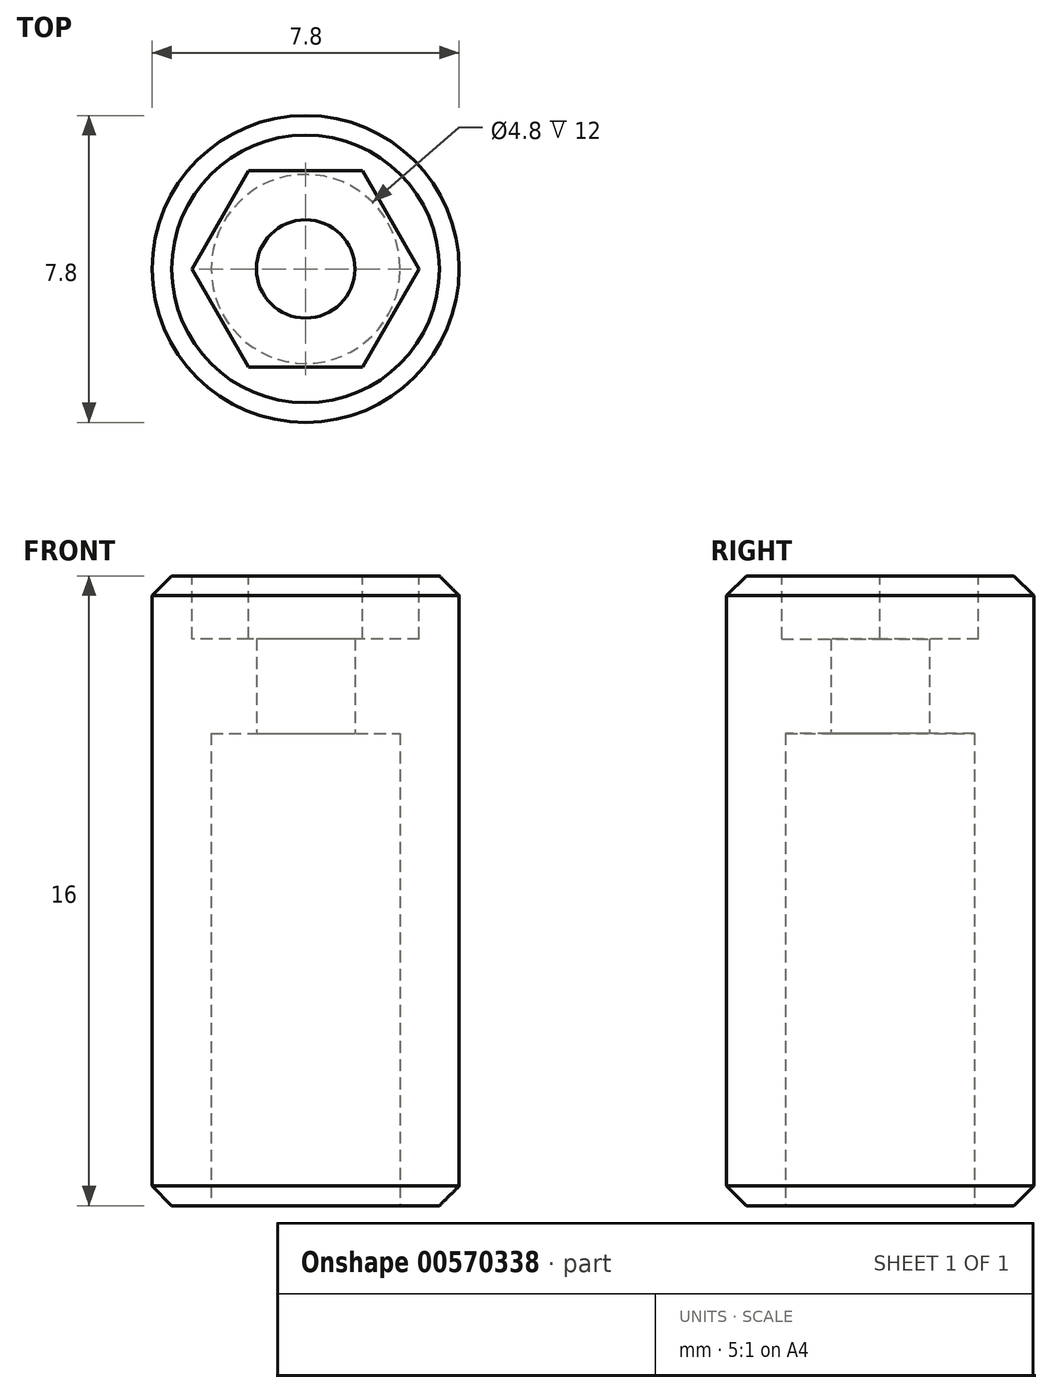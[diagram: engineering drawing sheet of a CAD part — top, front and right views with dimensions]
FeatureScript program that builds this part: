
annotation { "Feature Type Name" : "Feature", "Feature Type Description" : "" }
export const myFeature = defineFeature(function(context is Context, id is Id, definition is map)
    precondition{}
    {
        {
            var Q0;
            Q0=qCreatedBy(makeId("Top.planeOp"),FACE);
            var sketch = newSketch(context, id + "F0", { "sketchPlane" : qUnion([Q0])});
            skCircle(sketch, "E0", {"center": v(0, 0) * mm, "radius": 3.9 * mm});
            skSolve(sketch);
        }
        {
            var Q0;
            Q0 = qSketchRegion(id + "F0", true);
            extrude(context, id + "F1", {"entities" : qUnion([Q0]), "depth" : 16 * mm, "offsetDistance" : 25 * mm});
        }
        {
            var Q0;
            Q0=makeQuery(id+"F1.opExtrude","CAP_FACE",FACE,{"disambiguationData":[OSD([sQuery(id+"F0.wireOp",EDGE,"E0")])],"isStart":true});
            var sketch = newSketch(context, id + "F2", { "sketchPlane" : qUnion([Q0])});
            skCircle(sketch, "E1", {"center": v(0, 0) * mm, "radius": 2.4 * mm});
            skSolve(sketch);
        }
        {
            var Q0;
            Q0 = qSketchRegion(id + "F2", true);
            extrude(context, id + "F3", {"entities" : qUnion([Q0]), "operationType" : NewBodyOperationType.REMOVE, "oppositeDirection" : true, "depth" : 12 * mm, "offsetDistance" : 25 * mm});
        }
        {
            var Q0;
            Q0=makeQuery(id+"F3.boolean.opBoolean","COPY",FACE,{"derivedFrom":makeQuery(id+"F3.opExtrude","CAP_FACE",FACE,{"disambiguationData":[OSD([sQuery(id+"F2.wireOp",EDGE,"E1")])],"isStart":false})});
            var sketch = newSketch(context, id + "F4", { "sketchPlane" : qUnion([Q0])});
            skCircle(sketch, "E2", {"center": v(0, 0) * mm, "radius": 1.25 * mm});
            skSolve(sketch);
        }
        {
            var Q0;
            Q0 = qSketchRegion(id + "F4", true);
            extrude(context, id + "F5", {"entities" : qUnion([Q0]), "operationType" : NewBodyOperationType.REMOVE, "endBound" : BoundingType.THROUGH_ALL, "oppositeDirection" : true, "depth" : 25 * mm, "offsetDistance" : 25 * mm});
        }
        {
            var Q0;
            Q0=makeQuery(id+"F1.opExtrude","CAP_EDGE",EDGE,{"disambiguationData":[OSD([sQuery(id+"F0.wireOp",EDGE,"E0")])],"isStart":false});
            chamfer(context, id + "F6", {"entities" : qUnion([Q0]), "width" : .5 * mm, "tangentPropagation" : true});
        }
        {
            var Q0;
            Q0=makeQuery(id+"F1.opExtrude","CAP_EDGE",EDGE,{"disambiguationData":[OSD([sQuery(id+"F0.wireOp",EDGE,"E0")])],"isStart":true});
            chamfer(context, id + "F7", {"entities" : qUnion([Q0]), "width" : .5 * mm, "tangentPropagation" : true});
        }
        {
            var Q0;
            Q0=makeQuery(id+"F1.opExtrude","CAP_FACE",FACE,{"disambiguationData":[OSD([sQuery(id+"F0.wireOp",EDGE,"E0")])],"isStart":false});
            var sketch = newSketch(context, id + "F8", { "sketchPlane" : qUnion([Q0])});
            skCircle(sketch, "E3.cCircle", {"center": v(0, 0) * mm, "radius": 2.89 * mm, "construction": true});
            skLineSegment(sketch, "E3.0", {"start": v(-1.44, -2.5) * mm, "end": v(-2.89, 0) * mm});
            skLineSegment(sketch, "E3.1", {"start": v(-2.89, 0) * mm, "end": v(-1.44, 2.5) * mm});
            skLineSegment(sketch, "E3.2", {"start": v(-1.44, 2.5) * mm, "end": v(1.44, 2.5) * mm});
            skLineSegment(sketch, "E3.3", {"start": v(1.44, 2.5) * mm, "end": v(2.89, 0) * mm});
            skLineSegment(sketch, "E3.4", {"start": v(2.89, 0) * mm, "end": v(1.44, -2.5) * mm});
            skLineSegment(sketch, "E3.5", {"start": v(1.44, -2.5) * mm, "end": v(-1.44, -2.5) * mm});
            skSolve(sketch);
        }
        {
            var Q0;
            Q0 = qSketchRegion(id + "F8", true);
            extrude(context, id + "F9", {"entities" : qUnion([Q0]), "operationType" : NewBodyOperationType.REMOVE, "oppositeDirection" : true, "depth" : 1.6 * mm, "offsetDistance" : 25 * mm});
        }
    });
